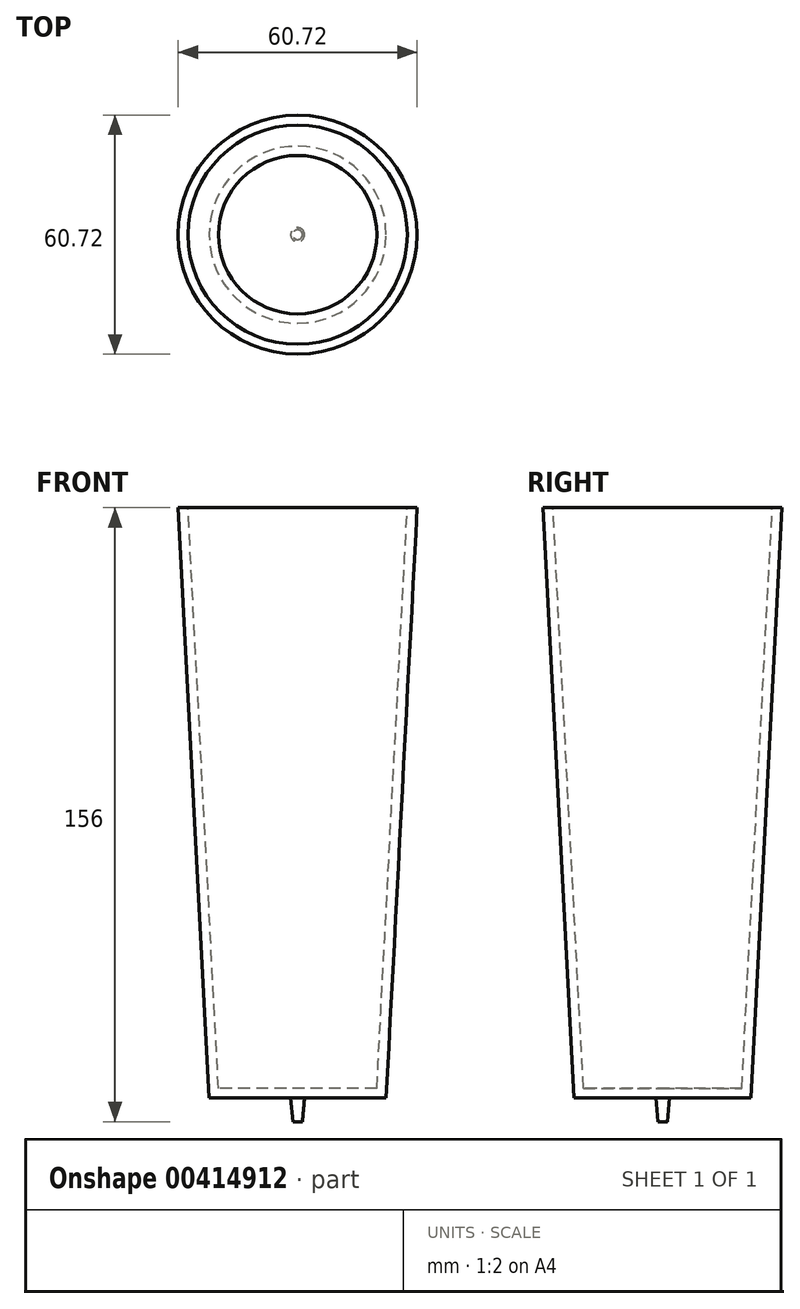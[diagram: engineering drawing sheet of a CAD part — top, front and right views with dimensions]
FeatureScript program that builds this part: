
annotation { "Feature Type Name" : "Feature", "Feature Type Description" : "" }
export const myFeature = defineFeature(function(context is Context, id is Id, definition is map)
    precondition{}
    {
        {
            var Q0;
            Q0=qCreatedBy(makeId("Top.planeOp"),FACE);
            var sketch = newSketch(context, id + "F0", { "sketchPlane" : qUnion([Q0])});
            skCircle(sketch, "E0", {"center": v(0, 0) * mm, "radius": 22.5 * mm});
            skSolve(sketch);
        }
        {
            var Q0;
            Q0=makeQuery(id+"F0.imprint","IMPRINT",FACE,{"disambiguationData":[TD([[makeQuery(id+"F0.imprint","IMPRINT",EDGE,{"derivedFrom":sQuery(id+"F0.wireOp",EDGE,"E0")}),1.0]])]});
            extrude(context, id + "F1", {"entities" : qUnion([Q0]), "depth" : 150 * mm, "hasDraft" : true, "draftAngle" : 3 * degree});
        }
        {
            var Q0;
            Q0=makeQuery(id+"F1.opExtrude","CAP_FACE",FACE,{"disambiguationData":[OSD([sQuery(id+"F0.wireOp",EDGE,"E0")])],"isStart":false});
            shell(context, id + "F2", {"entities" : qUnion([Q0]), "thickness" : 2.5 * mm});
        }
        {
            var Q0;
            Q0=qCreatedBy(makeId("Top.planeOp"),FACE);
            var sketch = newSketch(context, id + "F3", { "sketchPlane" : qUnion([Q0])});
            skCircle(sketch, "E1", {"center": v(0, 0) * mm, "radius": 1.75 * mm});
            skSolve(sketch);
        }
        {
            var Q0;
            Q0=makeQuery(id+"F3.imprint","IMPRINT",FACE,{"disambiguationData":[TD([[makeQuery(id+"F3.imprint","IMPRINT",EDGE,{"derivedFrom":sQuery(id+"F3.wireOp",EDGE,"E1")}),1.0]])]});
            extrude(context, id + "F4", {"entities" : qUnion([Q0]), "operationType" : NewBodyOperationType.ADD, "oppositeDirection" : true, "depth" : 6 * mm, "hasDraft" : true, "draftAngle" : 5 * degree, "draftPullDirection" : true});
        }
    });
